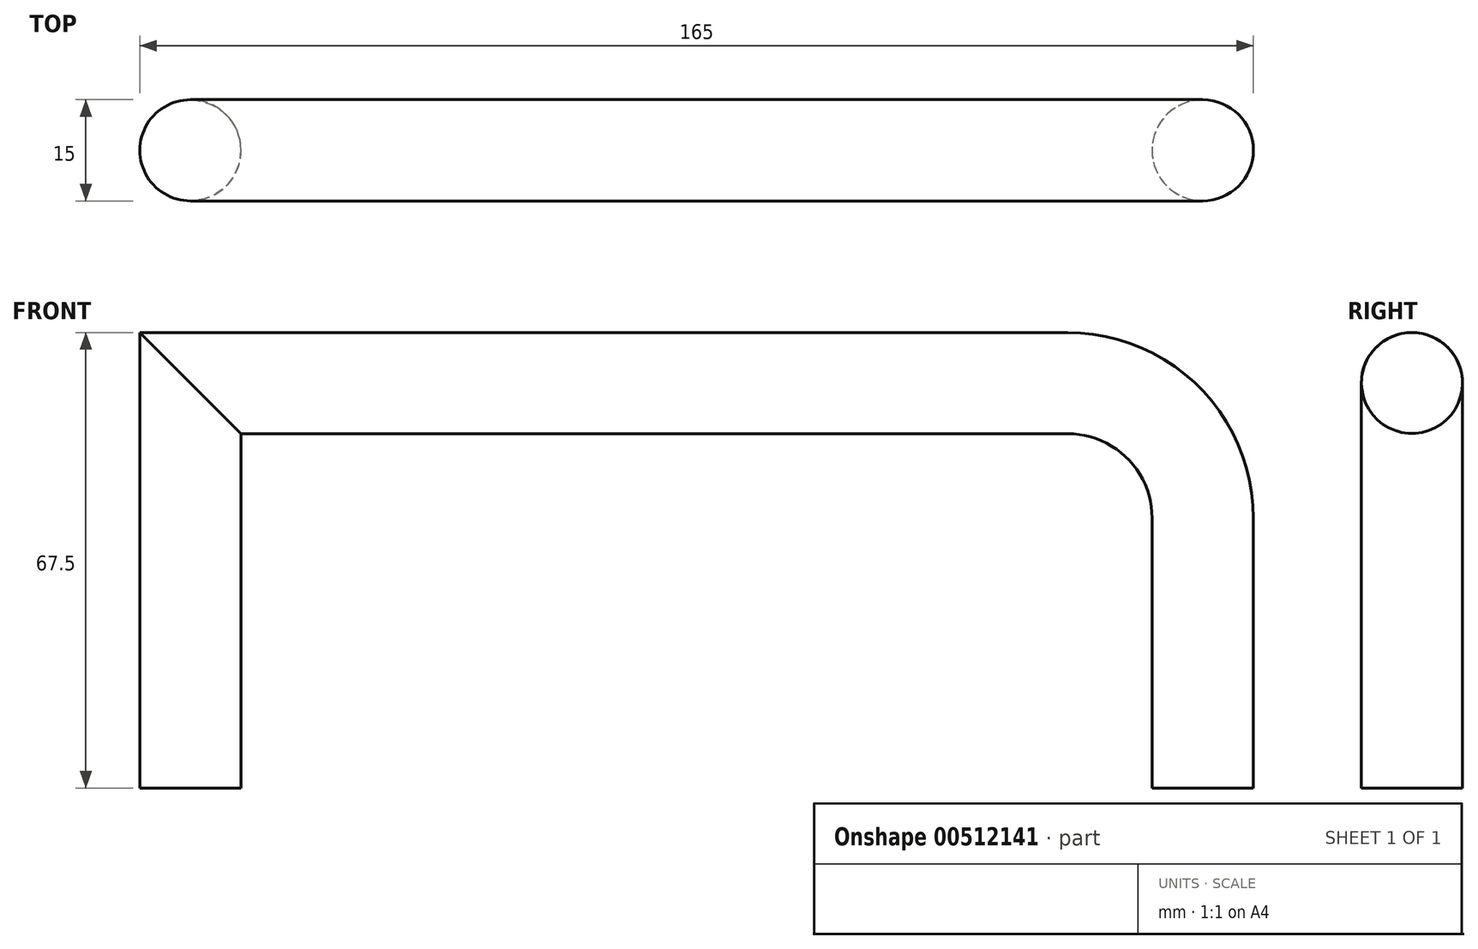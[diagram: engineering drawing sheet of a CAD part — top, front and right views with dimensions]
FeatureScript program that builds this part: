
annotation { "Feature Type Name" : "Feature", "Feature Type Description" : "" }
export const myFeature = defineFeature(function(context is Context, id is Id, definition is map)
    precondition{}
    {
        {
            var Q0;
            Q0=qCreatedBy(makeId("Front.planeOp"),FACE);
            var sketch = newSketch(context, id + "F0", { "sketchPlane" : qUnion([Q0])});
            skLineSegment(sketch, "E0", {"start": v(-75, 0) * mm, "end": v(-75, 60) * mm});
            skLineSegment(sketch, "E1", {"start": v(-75, 60) * mm, "end": v(55, 60) * mm});
            skLineSegment(sketch, "E2", {"start": v(75, 40) * mm, "end": v(75, 0) * mm});
            skPoint(sketch, "E3.visualSharp", {"position": v(75, 60) * mm});
            skArc(sketch, "E3.filletArc", {"start": v(75, 40) * mm, "mid": v(69.14, 54.14) * mm, "end": v(55, 60) * mm});
            skSolve(sketch);
        }
        {
            var Q0;
            Q0=qCreatedBy(makeId("Top.planeOp"),FACE);
            var sketch = newSketch(context, id + "F1", { "sketchPlane" : qUnion([Q0])});
            skCircle(sketch, "E4", {"center": v(75, 0) * mm, "radius": 7.5 * mm});
            skCircle(sketch, "E5.cCircle", {"center": v(-75, 0) * mm, "radius": 10 * mm, "construction": true});
            skLineSegment(sketch, "E5.0", {"start": v(-77.48, 12.11) * mm, "end": v(-64.25, 6.1) * mm});
            skLineSegment(sketch, "E5.1", {"start": v(-64.25, 6.1) * mm, "end": v(-65.88, -8.34) * mm});
            skLineSegment(sketch, "E5.2", {"start": v(-65.88, -8.34) * mm, "end": v(-80.11, -11.25) * mm});
            skLineSegment(sketch, "E5.3", {"start": v(-80.11, -11.25) * mm, "end": v(-87.28, 1.39) * mm});
            skLineSegment(sketch, "E5.4", {"start": v(-87.28, 1.39) * mm, "end": v(-77.48, 12.11) * mm});
            skPoint(sketch, "E5.0.midPoint", {"position": v(-70.86, 9.1) * mm});
            skSolve(sketch);
        }
        {
            var Q0;
            Q0=makeQuery(id+"F1.imprint","IMPRINT",FACE,{"disambiguationData":[TD([[makeQuery(id+"F1.imprint","IMPRINT",EDGE,{"derivedFrom":sQuery(id+"F1.wireOp",EDGE,"E4")}),1.0]])]});
            var Q1;
            Q1 = qConstructionFilter(qBodyType(qCreatedBy(id + "F0" ,EDGE), BodyType.WIRE), ConstructionObject.NO);
            sweep(context, id + "F2", {"profiles" : qUnion([Q0]), "path" : qUnion([Q1])});
        }
    });
